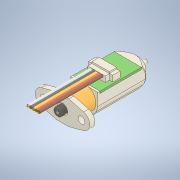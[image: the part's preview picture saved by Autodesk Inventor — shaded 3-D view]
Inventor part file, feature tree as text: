
AUTODESK INVENTOR PART (.ipt)
format: ipt  version: 2022 (Build 260153000, 153)  size: 858,112 bytes
history: imported  units: in
note: dims shown in document units (in); Inventor stores cm internally (conversion verified against a paired STEP export)
features: sketch x5, imported_body x1
ambient origin geometry x8: Origin, YZ Plane, XZ Plane, XY Plane, X Axis, Y Axis, Z Axis, Center Point
bodies: Solid1 (imported_parasolid), Body1 (imported_parasolid)
feature tree (6):
  sketch  "Sketch1"
  sketch  "Sketch2"
  sketch  "Sketch3"
  sketch  "Sketch4"
  sketch  "Sketch5"
  imported_body  NMx_Import_Brep_tag  [imported B-rep: ~8 faces, bbox_mm=[0.0, 0.0, 1.0]]
